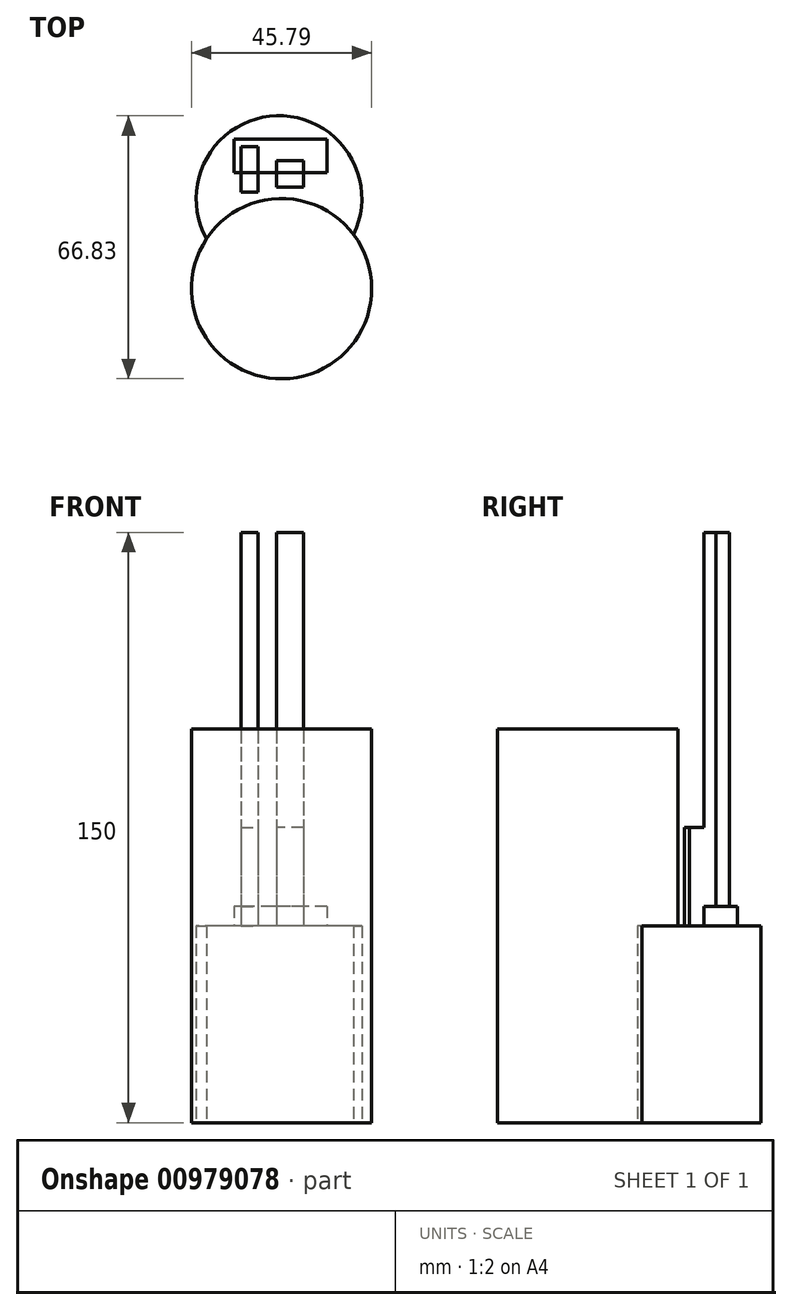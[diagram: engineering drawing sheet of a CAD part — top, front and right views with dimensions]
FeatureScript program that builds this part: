
annotation { "Feature Type Name" : "Feature", "Feature Type Description" : "" }
export const myFeature = defineFeature(function(context is Context, id is Id, definition is map)
    precondition{}
    {
        {
            var Q0;
            Q0=qCreatedBy(makeId("Top.planeOp"),FACE);
            var sketch = newSketch(context, id + "F0", { "sketchPlane" : qUnion([Q0])});
            skCircle(sketch, "E0", {"center": v(-37.01, -36.03) * mm, "radius": 22.9 * mm});
            skCircle(sketch, "E1", {"center": v(-37.68, -13.14) * mm, "radius": 21.05 * mm});
            skSolve(sketch);
        }
        {
            var Q0;
            {var subQ0=sQuery(id+"F0.wireOp",EDGE,"E1");var subQ1=sQuery(id+"F0.wireOp",EDGE,"E0");var subQ2=makeQuery(id+"F0.imprint","INTERSECT",VERTEX,{"disambiguationData":[OD(0.0)],"derivedFrom":[subQ1,subQ0]});Q0=makeQuery(id+"F0.imprint","IMPRINT",FACE,{"disambiguationData":[TD([[makeQuery(id+"F0.imprint","IMPRINT",EDGE,{"disambiguationData":[TD([[subQ2,-1.0]])],"derivedFrom":subQ1}),1.0]])]});}
            var Q1;
            {var subQ0=sQuery(id+"F0.wireOp",EDGE,"E1");var subQ1=sQuery(id+"F0.wireOp",EDGE,"E0");var subQ2=makeQuery(id+"F0.imprint","INTERSECT",VERTEX,{"disambiguationData":[OD(0.0)],"derivedFrom":[subQ1,subQ0]});Q1=makeQuery(id+"F0.imprint","IMPRINT",FACE,{"disambiguationData":[TD([[makeQuery(id+"F0.imprint","IMPRINT",EDGE,{"disambiguationData":[TD([[subQ2,1.0]])],"derivedFrom":subQ1}),1.0]])]});}
            extrude(context, id + "F1", {"entities" : qUnion([Q0, Q1]), "depth" : 100 * mm, "offsetDistance" : 25 * mm});
        }
        {
            var Q0;
            {var subQ0=sQuery(id+"F0.wireOp",EDGE,"E1");var subQ1=sQuery(id+"F0.wireOp",EDGE,"E0");var subQ2=makeQuery(id+"F0.imprint","INTERSECT",VERTEX,{"disambiguationData":[OD(0.0)],"derivedFrom":[subQ1,subQ0]});Q0=makeQuery(id+"F0.imprint","IMPRINT",FACE,{"disambiguationData":[TD([[makeQuery(id+"F0.imprint","IMPRINT",EDGE,{"disambiguationData":[TD([[subQ2,1.0]])],"derivedFrom":subQ1}),-1.0]])]});}
            extrude(context, id + "F2", {"entities" : qUnion([Q0]), "operationType" : NewBodyOperationType.ADD, "depth" : 50 * mm, "offsetDistance" : 25 * mm});
        }
        {
            var Q0;
            Q0=makeQuery(id+"F2.opExtrude","CAP_FACE",FACE,{"disambiguationData":[OSD([sQuery(id+"F0.wireOp",EDGE,"E0"),sQuery(id+"F0.wireOp",EDGE,"E1")])],"isStart":false});
            var sketch = newSketch(context, id + "F3", { "sketchPlane" : qUnion([Q0])});
            skLineSegment(sketch, "E2.bottom", {"start": v(-25.5, -6.55) * mm, "end": v(-49.14, -6.55) * mm});
            skLineSegment(sketch, "E2.top", {"start": v(-25.5, 2.01) * mm, "end": v(-49.14, 2.01) * mm});
            skLineSegment(sketch, "E2.left", {"start": v(-25.5, -6.55) * mm, "end": v(-25.5, 2.01) * mm});
            skLineSegment(sketch, "E2.right", {"start": v(-49.14, -6.55) * mm, "end": v(-49.14, 2.01) * mm});
            skLineSegment(sketch, "E3.bottom", {"start": v(-31.5, -10.22) * mm, "end": v(-38.32, -10.22) * mm});
            skLineSegment(sketch, "E3.top", {"start": v(-31.5, -3.46) * mm, "end": v(-38.32, -3.46) * mm});
            skLineSegment(sketch, "E3.left", {"start": v(-31.5, -10.22) * mm, "end": v(-31.5, -3.46) * mm});
            skLineSegment(sketch, "E3.right", {"start": v(-38.32, -10.22) * mm, "end": v(-38.32, -3.46) * mm});
            skLineSegment(sketch, "E4.bottom", {"start": v(-47.26, -11.5) * mm, "end": v(-43.01, -11.5) * mm});
            skLineSegment(sketch, "E4.top", {"start": v(-47.26, 0) * mm, "end": v(-43.01, 0) * mm});
            skLineSegment(sketch, "E4.left", {"start": v(-47.26, -11.5) * mm, "end": v(-47.26, 0) * mm});
            skLineSegment(sketch, "E4.right", {"start": v(-43.01, -11.5) * mm, "end": v(-43.01, 0) * mm});
            skSolve(sketch);
        }
        {
            var Q0;
            {var subQ5=sQuery(id+"F3.wireOp",EDGE,"E3.bottom");Q0=makeQuery(id+"F3.imprint","IMPRINT",FACE,{"disambiguationData":[TD([[makeQuery(id+"F3.imprint","IMPRINT",EDGE,{"derivedFrom":subQ5}),-1.0]])]});}
            var Q1;
            {var subQ5=sQuery(id+"F3.wireOp",EDGE,"E4.bottom");Q1=makeQuery(id+"F3.imprint","IMPRINT",FACE,{"disambiguationData":[TD([[makeQuery(id+"F3.imprint","IMPRINT",EDGE,{"derivedFrom":subQ5}),1.0]])]});}
            extrude(context, id + "F4", {"entities" : qUnion([Q0, Q1]), "operationType" : NewBodyOperationType.ADD, "depth" : 25 * mm, "offsetDistance" : 25 * mm});
        }
        {
            var Q0;
            {var subQ5=sQuery(id+"F3.wireOp",EDGE,"E3.top");Q0=makeQuery(id+"F3.imprint","IMPRINT",FACE,{"disambiguationData":[TD([[makeQuery(id+"F3.imprint","IMPRINT",EDGE,{"derivedFrom":subQ5}),1.0]])]});}
            var Q1;
            {var subQ5=sQuery(id+"F3.wireOp",EDGE,"E4.top");Q1=makeQuery(id+"F3.imprint","IMPRINT",FACE,{"disambiguationData":[TD([[makeQuery(id+"F3.imprint","IMPRINT",EDGE,{"derivedFrom":subQ5}),-1.0]])]});}
            extrude(context, id + "F5", {"entities" : qUnion([Q0, Q1]), "operationType" : NewBodyOperationType.ADD, "depth" : 100 * mm, "offsetDistance" : 25 * mm});
        }
        {
            var Q0;
            Q0=makeQuery(id+"F3.imprint","IMPRINT",FACE,{"disambiguationData":[TD([[makeQuery(id+"F3.imprint","IMPRINT",EDGE,{"derivedFrom":sQuery(id+"F3.wireOp",EDGE,"E2.top")}),1.0]])]});
            extrude(context, id + "F6", {"entities" : qUnion([Q0]), "operationType" : NewBodyOperationType.ADD, "depth" : 5 * mm, "offsetDistance" : 25 * mm});
        }
    });
